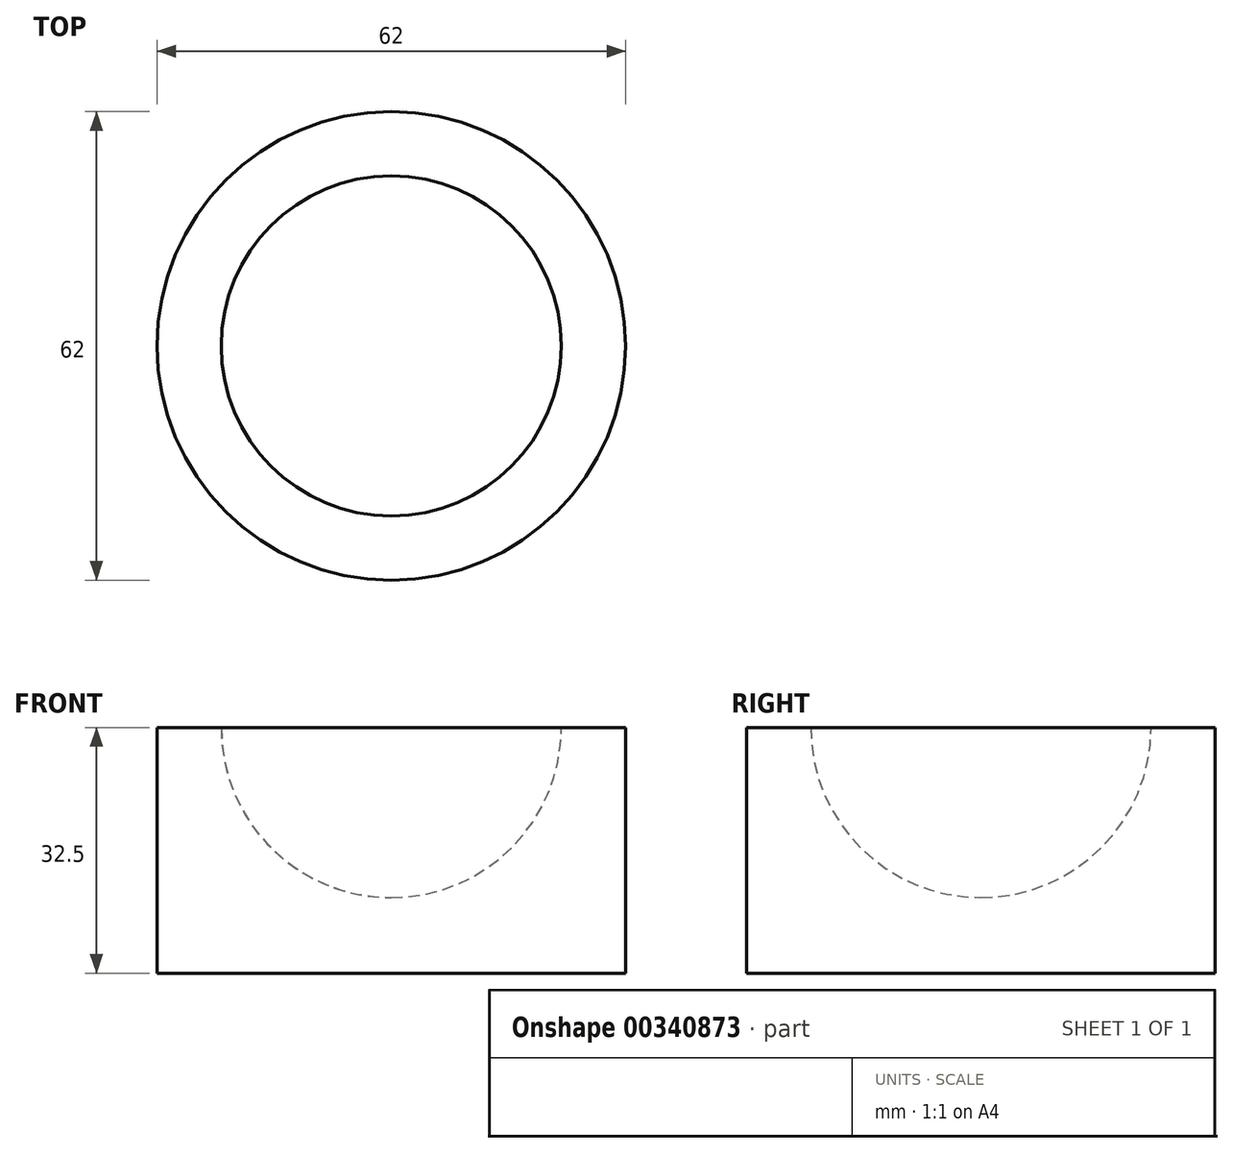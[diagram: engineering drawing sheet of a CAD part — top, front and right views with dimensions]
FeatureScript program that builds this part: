
annotation { "Feature Type Name" : "Feature", "Feature Type Description" : "" }
export const myFeature = defineFeature(function(context is Context, id is Id, definition is map)
    precondition{}
    {
        {
            var Q0;
            Q0=qCreatedBy(makeId("Front.planeOp"),FACE);
            var sketch = newSketch(context, id + "F0", { "sketchPlane" : qUnion([Q0])});
            skLineSegment(sketch, "E0.bottom", {"start": v(0, 0) * mm, "end": v(31, 0) * mm});
            skLineSegment(sketch, "E0.top", {"start": v(22.5, 32.5) * mm, "end": v(31, 32.5) * mm});
            skLineSegment(sketch, "E0.left", {"start": v(0, 0) * mm, "end": v(0, 10) * mm});
            skLineSegment(sketch, "E0.right", {"start": v(31, 0) * mm, "end": v(31, 32.5) * mm});
            skArc(sketch, "E1", {"start": v(0, 10) * mm, "mid": v(15.9, 16.6) * mm, "end": v(22.5, 32.5) * mm});
            skSolve(sketch);
        }
        {
            var Q0;
            Q0 = qSketchRegion(id + "F0", true);
            var Q1;
            Q1=sQuery(id+"F0.wireOp",EDGE,"E0.left");
            revolve(context, id + "F1", {"entities" : qUnion([Q0]), "axis" : qUnion([Q1]), "revolveType" : RevolveType.FULL});
        }
    });
